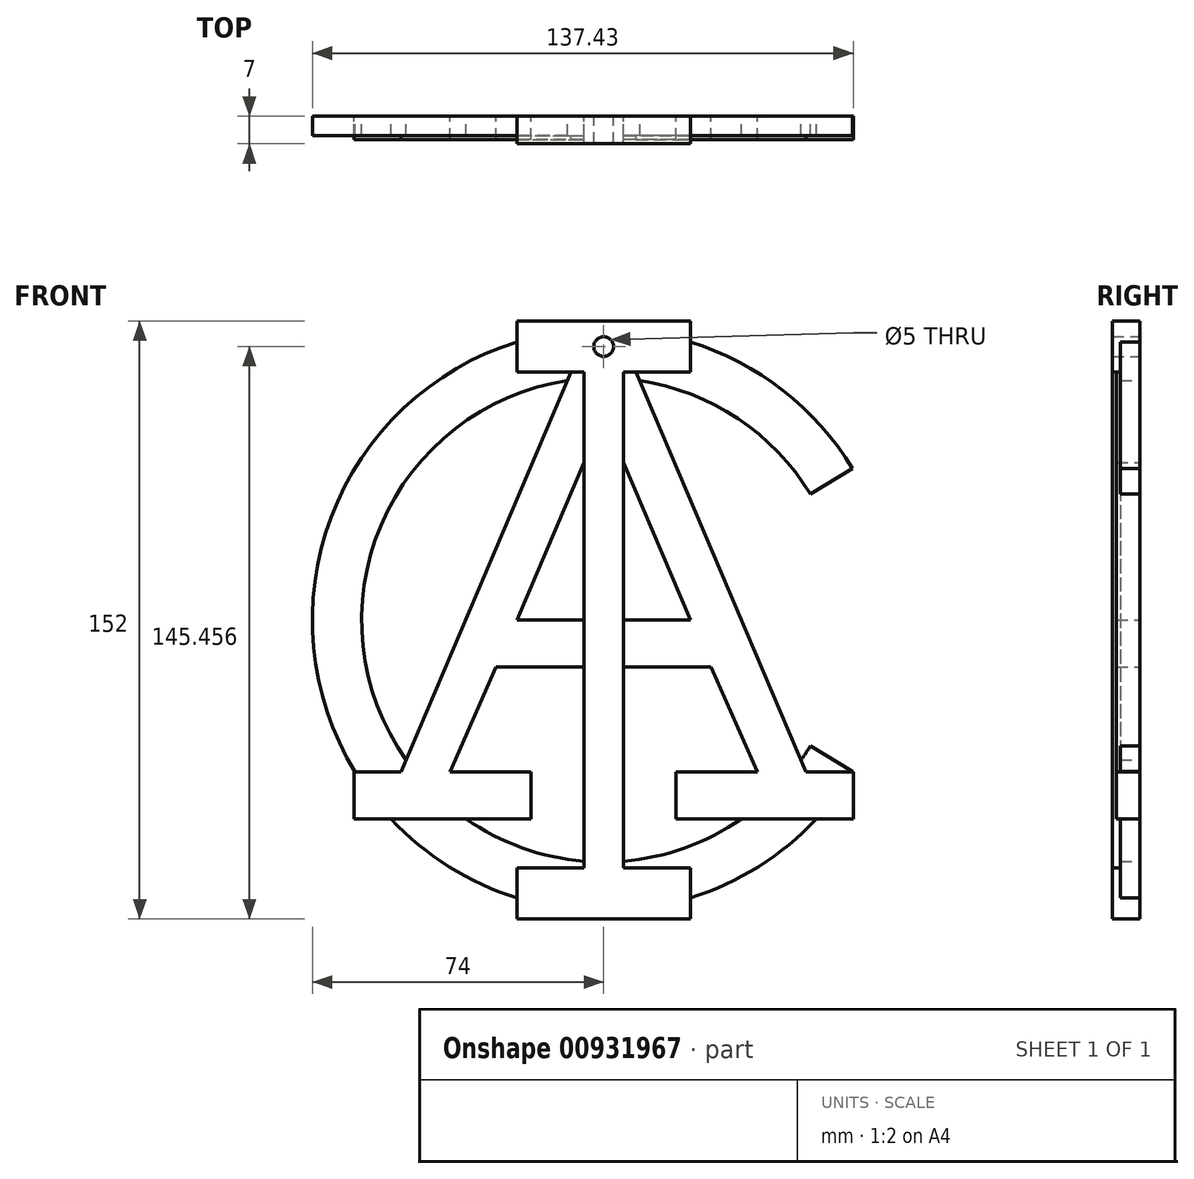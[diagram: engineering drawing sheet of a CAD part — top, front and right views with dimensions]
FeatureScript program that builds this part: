
annotation { "Feature Type Name" : "Feature", "Feature Type Description" : "" }
export const myFeature = defineFeature(function(context is Context, id is Id, definition is map)
    precondition{}
    {
        {
            var Q0;
            Q0=qCreatedBy(makeId("Front.planeOp"),FACE);
            var sketch = newSketch(context, id + "F0", { "sketchPlane" : qUnion([Q0])});
            skLineSegment(sketch, "E0", {"start": v(0, -76) * mm, "end": v(-22, -76) * mm});
            skLineSegment(sketch, "E1", {"start": v(-22, -76) * mm, "end": v(-22, -63) * mm});
            skLineSegment(sketch, "E2", {"start": v(-22, -63) * mm, "end": v(-5, -63) * mm});
            skLineSegment(sketch, "E3", {"start": v(-5, -63) * mm, "end": v(-5, 0) * mm});
            skLineSegment(sketch, "E4", {"start": v(0, 0) * mm, "end": v(-5, 0) * mm});
            skLineSegment(sketch, "E5.MirrorCS", {"start": v(0, 76) * mm, "end": v(-22, 76) * mm});
            skLineSegment(sketch, "E6.MirrorCS", {"start": v(-22, 76) * mm, "end": v(-22, 63) * mm});
            skLineSegment(sketch, "E7.MirrorCS", {"start": v(-22, 63) * mm, "end": v(-5, 63) * mm});
            skLineSegment(sketch, "E8", {"start": v(-5, 63) * mm, "end": v(-5, 0) * mm});
            skLineSegment(sketch, "E9", {"start": v(-5, 0) * mm, "end": v(-5, -63) * mm});
            skLineSegment(sketch, "E10", {"start": v(-5, 0) * mm, "end": v(-22, 0) * mm});
            skLineSegment(sketch, "E11", {"start": v(-22, 0) * mm, "end": v(-5, 40) * mm});
            skLineSegment(sketch, "E12", {"start": v(-35, 0.07) * mm, "end": v(-8.25, 63) * mm});
            skLineSegment(sketch, "E13", {"start": v(-27.3, -12) * mm, "end": v(-5, -12) * mm});
            skLineSegment(sketch, "E14", {"start": v(-35, 0.07) * mm, "end": v(-51.43, -38.58) * mm});
            skLineSegment(sketch, "E15", {"start": v(-27.3, -12) * mm, "end": v(-39.06, -38.58) * mm});
            skLineSegment(sketch, "E16", {"start": v(-51.43, -38.58) * mm, "end": v(-63.43, -38.58) * mm});
            skLineSegment(sketch, "E17", {"start": v(-63.43, -38.58) * mm, "end": v(-63.43, -50.58) * mm});
            skLineSegment(sketch, "E18", {"start": v(-63.43, -50.58) * mm, "end": v(-18.43, -50.58) * mm});
            skLineSegment(sketch, "E19", {"start": v(-18.43, -50.58) * mm, "end": v(-18.43, -38.58) * mm});
            skLineSegment(sketch, "E20", {"start": v(-18.43, -38.58) * mm, "end": v(-39.06, -38.58) * mm});
            skArc(sketch, "E21", {"start": v(52.54, 31.96) * mm, "mid": v(34.07, 51.2) * mm, "end": v(9.19, 60.81) * mm});
            skArc(sketch, "E22", {"start": v(63.22, 38.46) * mm, "mid": v(45.55, 58.32) * mm, "end": v(22, 70.65) * mm});
            skLineSegment(sketch, "E23.MirrorCS", {"start": v(0, 76) * mm, "end": v(22, 76) * mm});
            skLineSegment(sketch, "E24.MirrorCS", {"start": v(22, 76) * mm, "end": v(22, 63) * mm});
            skLineSegment(sketch, "E25.MirrorCS", {"start": v(22, 63) * mm, "end": v(5, 63) * mm});
            skLineSegment(sketch, "E26.MirrorCS", {"start": v(35, 0.07) * mm, "end": v(8.25, 63) * mm});
            skLineSegment(sketch, "E27.MirrorCS", {"start": v(22, 0) * mm, "end": v(5, 40) * mm});
            skLineSegment(sketch, "E28.MirrorCS", {"start": v(35, 0.07) * mm, "end": v(51.43, -38.58) * mm});
            skLineSegment(sketch, "E29.MirrorCS", {"start": v(27.3, -12) * mm, "end": v(5, -12) * mm});
            skLineSegment(sketch, "E30.MirrorCS", {"start": v(27.3, -12) * mm, "end": v(39.06, -38.58) * mm});
            skLineSegment(sketch, "E31.MirrorCS", {"start": v(18.43, -38.58) * mm, "end": v(39.06, -38.58) * mm});
            skLineSegment(sketch, "E32.MirrorCS", {"start": v(63.43, -50.58) * mm, "end": v(18.43, -50.58) * mm});
            skLineSegment(sketch, "E33.MirrorCS", {"start": v(63.43, -38.58) * mm, "end": v(63.43, -50.58) * mm});
            skLineSegment(sketch, "E34.MirrorCS", {"start": v(51.43, -38.58) * mm, "end": v(63.43, -38.58) * mm});
            skLineSegment(sketch, "E35.MirrorCS", {"start": v(18.43, -50.58) * mm, "end": v(18.43, -38.58) * mm});
            skLineSegment(sketch, "E36.MirrorCS", {"start": v(5, 63) * mm, "end": v(5, 0) * mm});
            skLineSegment(sketch, "E37.MirrorCS", {"start": v(5, 0) * mm, "end": v(5, -63) * mm});
            skLineSegment(sketch, "E38.MirrorCS", {"start": v(22, -63) * mm, "end": v(5, -63) * mm});
            skLineSegment(sketch, "E39.MirrorCS", {"start": v(22, -76) * mm, "end": v(22, -63) * mm});
            skLineSegment(sketch, "E40.MirrorCS", {"start": v(0, -76) * mm, "end": v(22, -76) * mm});
            skLineSegment(sketch, "E41", {"start": v(22, 0) * mm, "end": v(5, 0) * mm});
            skLineSegment(sketch, "E42.trimOffspring", {"start": v(52.54, 31.96) * mm, "end": v(63.43, 38.58) * mm});
            skLineSegment(sketch, "E43.trimOffspring", {"start": v(52.54, -31.96) * mm, "end": v(63.43, -38.58) * mm});
            skCircle(sketch, "E44", {"center": v(0, 69.46) * mm, "radius": 2.5 * mm});
            skArc(sketch, "E45.trimOffspring", {"start": v(22, -70.65) * mm, "mid": v(39.3, -62.7) * mm, "end": v(54.01, -50.58) * mm});
            skArc(sketch, "E46.trimOffspring", {"start": v(50.16, -35.6) * mm, "mid": v(51.38, -33.8) * mm, "end": v(52.54, -31.96) * mm});
            skArc(sketch, "E47.trimOffspring", {"start": v(63.15, -38.58) * mm, "mid": v(63.18, -38.52) * mm, "end": v(63.22, -38.46) * mm});
            skArc(sketch, "E48.trimOffspring", {"start": v(-34.98, -50.58) * mm, "mid": v(-20.7, -57.91) * mm, "end": v(-5, -61.3) * mm});
            skArc(sketch, "E49.trimOffspring", {"start": v(-9.19, 60.81) * mm, "mid": v(-56.6, 24.06) * mm, "end": v(-50.16, -35.6) * mm});
            skArc(sketch, "E50.trimOffspring", {"start": v(-22, 70.65) * mm, "mid": v(-69.25, 26.08) * mm, "end": v(-63.15, -38.58) * mm});
            skArc(sketch, "E51.trimOffspring", {"start": v(5, -61.3) * mm, "mid": v(20.7, -57.91) * mm, "end": v(34.98, -50.58) * mm});
            skArc(sketch, "E52.trimOffspring", {"start": v(-54.01, -50.58) * mm, "mid": v(-39.3, -62.7) * mm, "end": v(-22, -70.65) * mm});
            skSolve(sketch);
        }
        {
            var Q0;
            {var subQ22=sQuery(id+"F0.wireOp",EDGE,"E0");Q0=makeQuery(id+"F0.imprint","IMPRINT",FACE,{"disambiguationData":[TD([[makeQuery(id+"F0.imprint","IMPRINT",EDGE,{"derivedFrom":subQ22}),-1.0]])]});}
            extrude(context, id + "F1", {"entities" : qUnion([Q0]), "depth" : 7 * mm, "offsetDistance" : 25 * mm});
        }
        {
            var Q0;
            {var subQ16=sQuery(id+"F0.wireOp",EDGE,"E27.MirrorCS");Q0=makeQuery(id+"F0.imprint","IMPRINT",FACE,{"disambiguationData":[TD([[makeQuery(id+"F0.imprint","IMPRINT",EDGE,{"derivedFrom":subQ16}),-1.0]])]});}
            var Q1;
            {var subQ14=sQuery(id+"F0.wireOp",EDGE,"E10");Q1=makeQuery(id+"F0.imprint","IMPRINT",FACE,{"disambiguationData":[TD([[makeQuery(id+"F0.imprint","IMPRINT",EDGE,{"derivedFrom":subQ14}),1.0]])]});}
            extrude(context, id + "F2", {"entities" : qUnion([Q0, Q1]), "operationType" : NewBodyOperationType.ADD, "depth" : 6 * mm, "offsetDistance" : 25 * mm});
        }
        {
            var Q0;
            {var subQ6=sQuery(id+"F0.wireOp",EDGE,"E21");Q0=makeQuery(id+"F0.imprint","IMPRINT",FACE,{"disambiguationData":[TD([[makeQuery(id+"F0.imprint","IMPRINT",EDGE,{"derivedFrom":subQ6}),-1.0]])]});}
            var Q1;
            {var subQ3=sQuery(id+"F0.wireOp",EDGE,"E49.trimOffspring");Q1=makeQuery(id+"F0.imprint","IMPRINT",FACE,{"disambiguationData":[TD([[makeQuery(id+"F0.imprint","IMPRINT",EDGE,{"derivedFrom":subQ3}),-1.0]])]});}
            var Q2;
            {var subQ4=sQuery(id+"F0.wireOp",EDGE,"E2");Q2=makeQuery(id+"F0.imprint","IMPRINT",FACE,{"disambiguationData":[TD([[makeQuery(id+"F0.imprint","IMPRINT",EDGE,{"derivedFrom":subQ4}),1.0]])]});}
            var Q3;
            {var subQ1=sQuery(id+"F0.wireOp",EDGE,"E38.MirrorCS");Q3=makeQuery(id+"F0.imprint","IMPRINT",FACE,{"disambiguationData":[TD([[makeQuery(id+"F0.imprint","IMPRINT",EDGE,{"derivedFrom":subQ1}),-1.0]])]});}
            var Q4;
            {var subQ0=sQuery(id+"F0.wireOp",EDGE,"E46.trimOffspring");Q4=makeQuery(id+"F0.imprint","IMPRINT",FACE,{"disambiguationData":[TD([[makeQuery(id+"F0.imprint","IMPRINT",EDGE,{"derivedFrom":subQ0}),-1.0]])]});}
            extrude(context, id + "F3", {"entities" : qUnion([Q0, Q1, Q2, Q3, Q4]), "operationType" : NewBodyOperationType.ADD, "depth" : 5 * mm, "offsetDistance" : 25 * mm});
        }
    });
